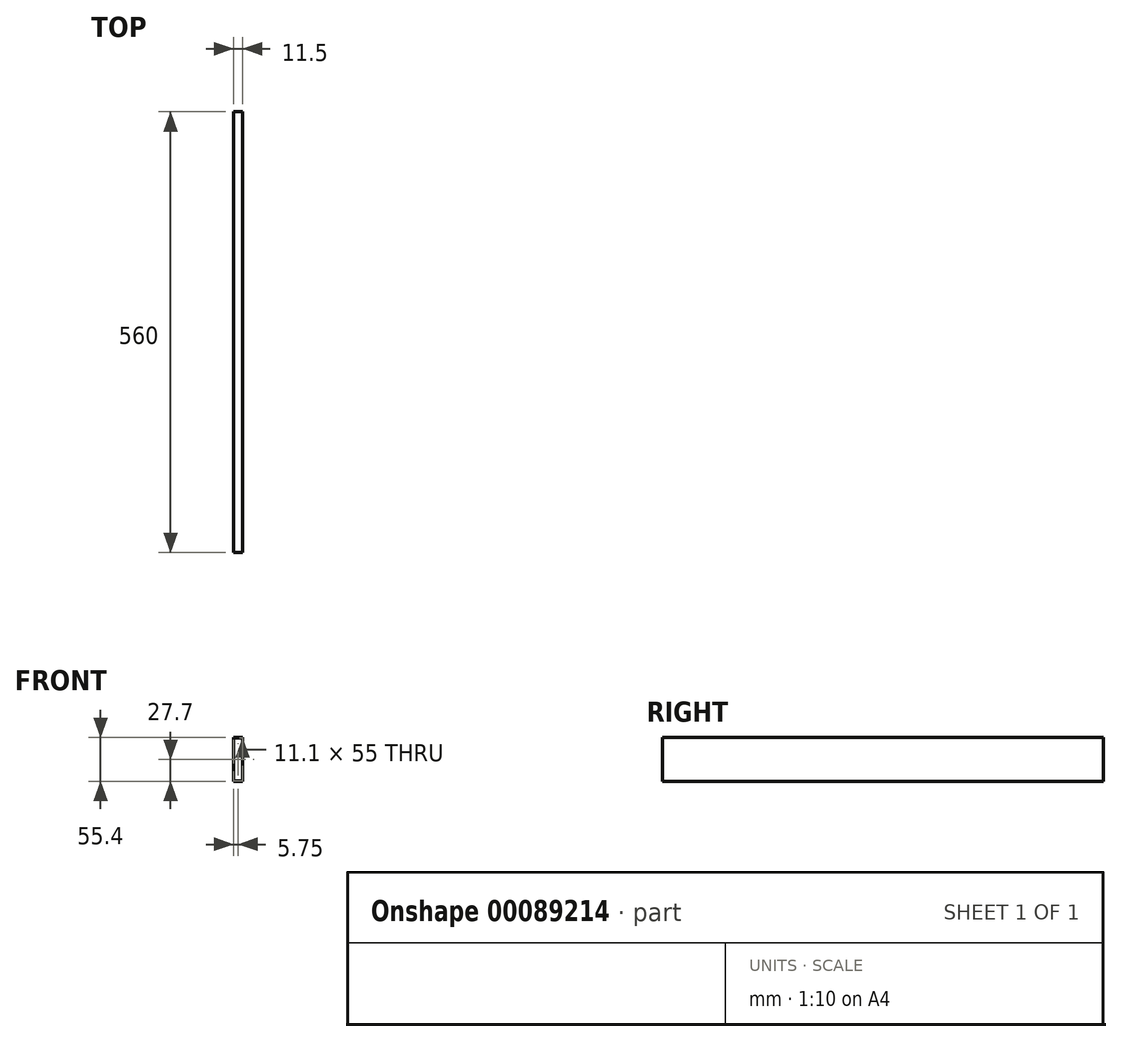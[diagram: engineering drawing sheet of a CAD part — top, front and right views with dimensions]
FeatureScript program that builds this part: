
annotation { "Feature Type Name" : "Feature", "Feature Type Description" : "" }
export const myFeature = defineFeature(function(context is Context, id is Id, definition is map)
    precondition{}
    {
        {
            var Q0;
            Q0=qCreatedBy(makeId("Front.planeOp"),FACE);
            var sketch = newSketch(context, id + "F0", { "sketchPlane" : qUnion([Q0])});
            skLineSegment(sketch, "E0.bottom", {"start": v(0, 0) * mm, "end": v(11.5, 0) * mm});
            skLineSegment(sketch, "E0.top", {"start": v(0, 55.4) * mm, "end": v(11.5, 55.4) * mm});
            skLineSegment(sketch, "E0.left", {"start": v(0, 0) * mm, "end": v(0, 55.4) * mm});
            skLineSegment(sketch, "E0.right", {"start": v(11.5, 0) * mm, "end": v(11.5, 55.4) * mm});
            skLineSegment(sketch, "E1.bottom", {"start": v(0.2, 55.2) * mm, "end": v(11.3, 55.2) * mm});
            skLineSegment(sketch, "E1.top", {"start": v(0.2, 0.2) * mm, "end": v(11.3, 0.2) * mm});
            skLineSegment(sketch, "E1.left", {"start": v(0.2, 55.2) * mm, "end": v(0.2, 0.2) * mm});
            skLineSegment(sketch, "E1.right", {"start": v(11.3, 55.2) * mm, "end": v(11.3, 0.2) * mm});
            skSolve(sketch);
        }
        {
            var Q0;
            Q0=makeQuery(id+"F0.imprint","IMPRINT",FACE,{"disambiguationData":[TD([[makeQuery(id+"F0.imprint","IMPRINT",EDGE,{"derivedFrom":sQuery(id+"F0.wireOp",EDGE,"E0.bottom")}),1.0]])]});
            extrude(context, id + "F1", {"entities" : qUnion([Q0]), "depth" : 560 * mm});
        }
    });
